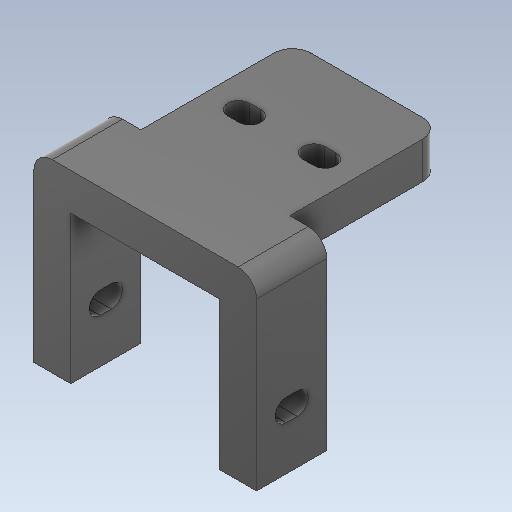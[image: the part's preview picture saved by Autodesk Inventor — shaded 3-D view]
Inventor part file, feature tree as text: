
AUTODESK INVENTOR PART (.ipt)
format: ipt  version: 2020 (Build 240168000, 168)  size: 190,464 bytes
history: native  units: mm
features: extrude x5, sketch x5, mirror x1, fillet x1
ambient origin geometry x8: Origin, YZ Plane, XZ Plane, XY Plane, X Axis, Y Axis, Z Axis, Center Point
bodies: Solid1 (feature_tree)
feature tree (12):
  extrude  "Extrusion1"  Depth=40.0mm
  extrude  "Extrusion2"  Depth=60.0mm TaperAngle=0.0deg
  extrude  "Extrusion4"  Depth=10.0mm
  mirror  "Mirror1"
  fillet  "Fillet1"  [1 undecoded]
  extrude  "Extrusion5"  Depth=5.0mm
  extrude  "Extrusion6"  Depth=6.0mm
  sketch  "Sketch1"  dims[d0=40.3mm d1=40.0mm]
  sketch  "Sketch3"  dims[d2=10.0mm d3=60.0mm d4=0.0mm]
  sketch  "Sketch5"  dims[d5=19.0mm d6=10.0mm d7=0.0mm d8=0.0mm]
  sketch  "Sketch9"  dims[d13=40.0mm d14=0.0mm d15=5.0mm]
  sketch  "Sketch10"  dims[d34=3.0mm d35=6.0mm d36=15.0mm d37=10.0mm d38=0.0mm d39=3.0mm d40=6.0mm d41=10.0mm d42=10.0mm d43=0.0mm d44=0.0mm]
note: 1 required parameter value undecoded (feature->parameter linkage not recoverable at this tier; creation-order binding heuristic only, values carry confidence <= 0.55)
